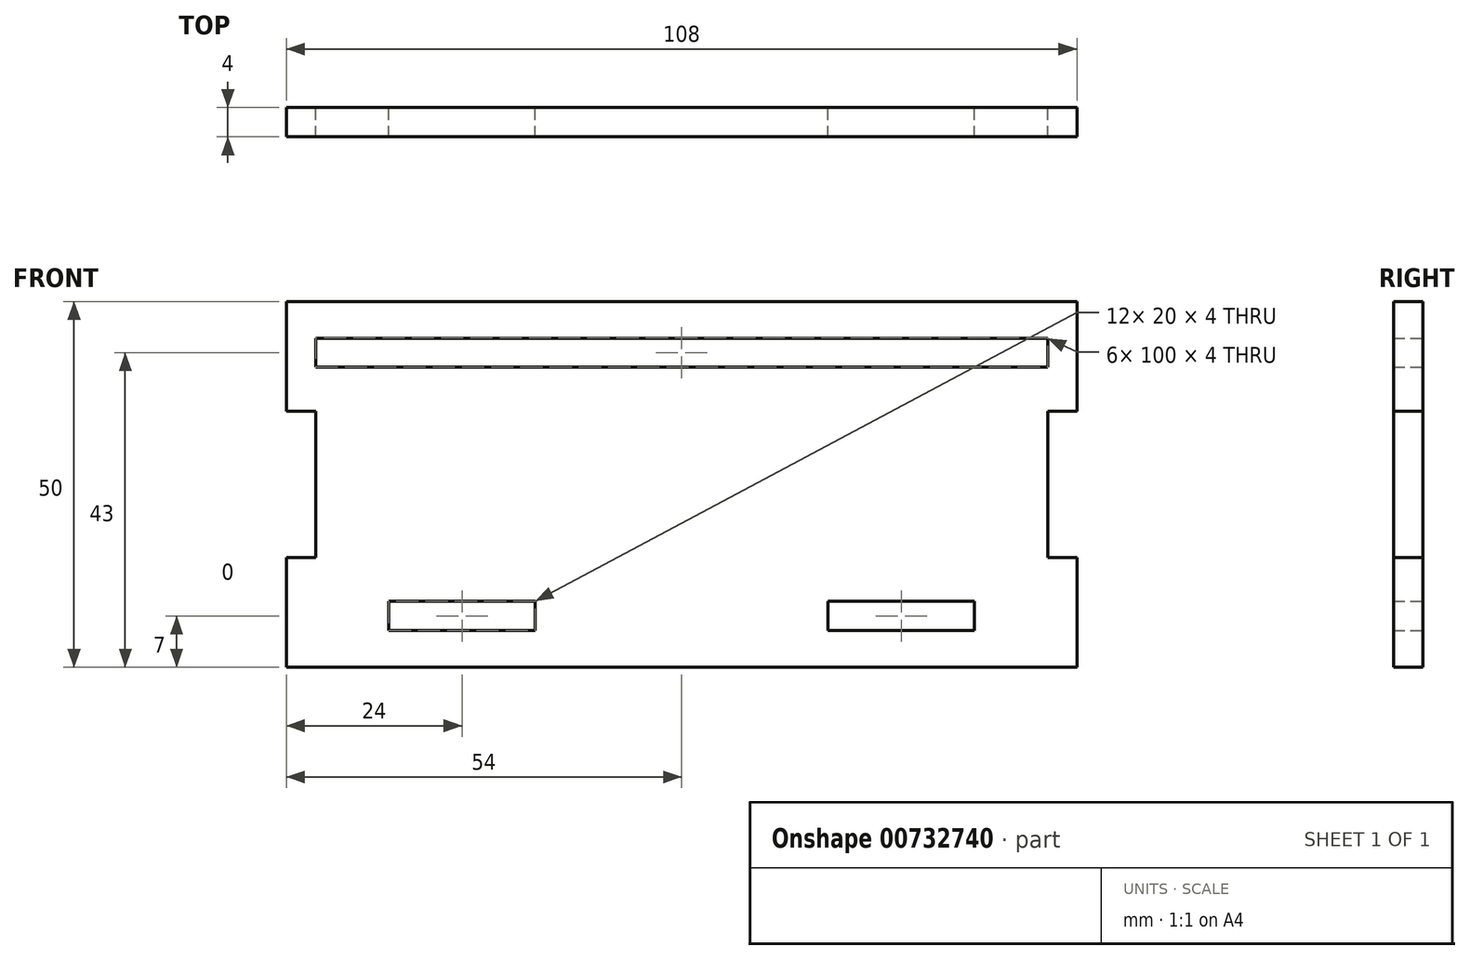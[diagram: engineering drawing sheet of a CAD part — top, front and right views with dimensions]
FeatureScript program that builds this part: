
annotation { "Feature Type Name" : "Feature", "Feature Type Description" : "" }
export const myFeature = defineFeature(function(context is Context, id is Id, definition is map)
    precondition{}
    {
        {
            var Q0;
            Q0=qCreatedBy(makeId("Front.planeOp"),FACE);
            var sketch = newSketch(context, id + "F0", { "sketchPlane" : qUnion([Q0])});
            skLineSegment(sketch, "E0.bottom", {"start": v(54, 25) * mm, "end": v(-54, 25) * mm});
            skLineSegment(sketch, "E0.top", {"start": v(54, -25) * mm, "end": v(-54, -25) * mm});
            skLineSegment(sketch, "E0.left", {"start": v(54, 25) * mm, "end": v(54, 10) * mm});
            skLineSegment(sketch, "E0.right", {"start": v(-54, 25) * mm, "end": v(-54, 10) * mm});
            skPoint(sketch, "E0.middle", {"position": v(0, 0) * mm});
            skLineSegment(sketch, "E1.bottom", {"start": v(-40, -16) * mm, "end": v(-20, -16) * mm});
            skLineSegment(sketch, "E1.top", {"start": v(-40, -20) * mm, "end": v(-20, -20) * mm});
            skLineSegment(sketch, "E1.left", {"start": v(-40, -16) * mm, "end": v(-40, -20) * mm});
            skLineSegment(sketch, "E1.right", {"start": v(-20, -16) * mm, "end": v(-20, -20) * mm});
            skLineSegment(sketch, "E2.MirrorCS", {"start": v(40, -16) * mm, "end": v(20, -16) * mm});
            skLineSegment(sketch, "E3.MirrorCS", {"start": v(40, -20) * mm, "end": v(20, -20) * mm});
            skLineSegment(sketch, "E4.MirrorCS", {"start": v(40, -16) * mm, "end": v(40, -20) * mm});
            skLineSegment(sketch, "E5.MirrorCS", {"start": v(20, -16) * mm, "end": v(20, -20) * mm});
            skLineSegment(sketch, "E6.bottom", {"start": v(-54, 10) * mm, "end": v(-50, 10) * mm});
            skLineSegment(sketch, "E6.top", {"start": v(-54, -10) * mm, "end": v(-50, -10) * mm});
            skLineSegment(sketch, "E6.right", {"start": v(-50, 10) * mm, "end": v(-50, -10) * mm});
            skLineSegment(sketch, "E7.MirrorCS", {"start": v(54, -10) * mm, "end": v(50, -10) * mm});
            skLineSegment(sketch, "E8.MirrorCS", {"start": v(50, 10) * mm, "end": v(50, -10) * mm});
            skLineSegment(sketch, "E9.MirrorCS", {"start": v(54, 10) * mm, "end": v(50, 10) * mm});
            skLineSegment(sketch, "E10.trimOffspring", {"start": v(-54, -10) * mm, "end": v(-54, -25) * mm});
            skLineSegment(sketch, "E11.trimOffspring", {"start": v(54, -10) * mm, "end": v(54, -25) * mm});
            skLineSegment(sketch, "E12.bottom", {"start": v(-50, 20) * mm, "end": v(50, 20) * mm});
            skLineSegment(sketch, "E12.top", {"start": v(-50, 16) * mm, "end": v(50, 16) * mm});
            skLineSegment(sketch, "E12.left", {"start": v(-50, 20) * mm, "end": v(-50, 16) * mm});
            skLineSegment(sketch, "E12.right", {"start": v(50, 20) * mm, "end": v(50, 16) * mm});
            skSolve(sketch);
        }
        {
            var Q0;
            Q0=makeQuery(id+"F0.imprint","IMPRINT",FACE,{"disambiguationData":[TD([[makeQuery(id+"F0.imprint","IMPRINT",EDGE,{"derivedFrom":sQuery(id+"F0.wireOp",EDGE,"E0.bottom")}),1.0]])]});
            extrude(context, id + "F1", {"entities" : qUnion([Q0]), "depth" : 4 * mm, "offsetDistance" : 25 * mm});
        }
    });
